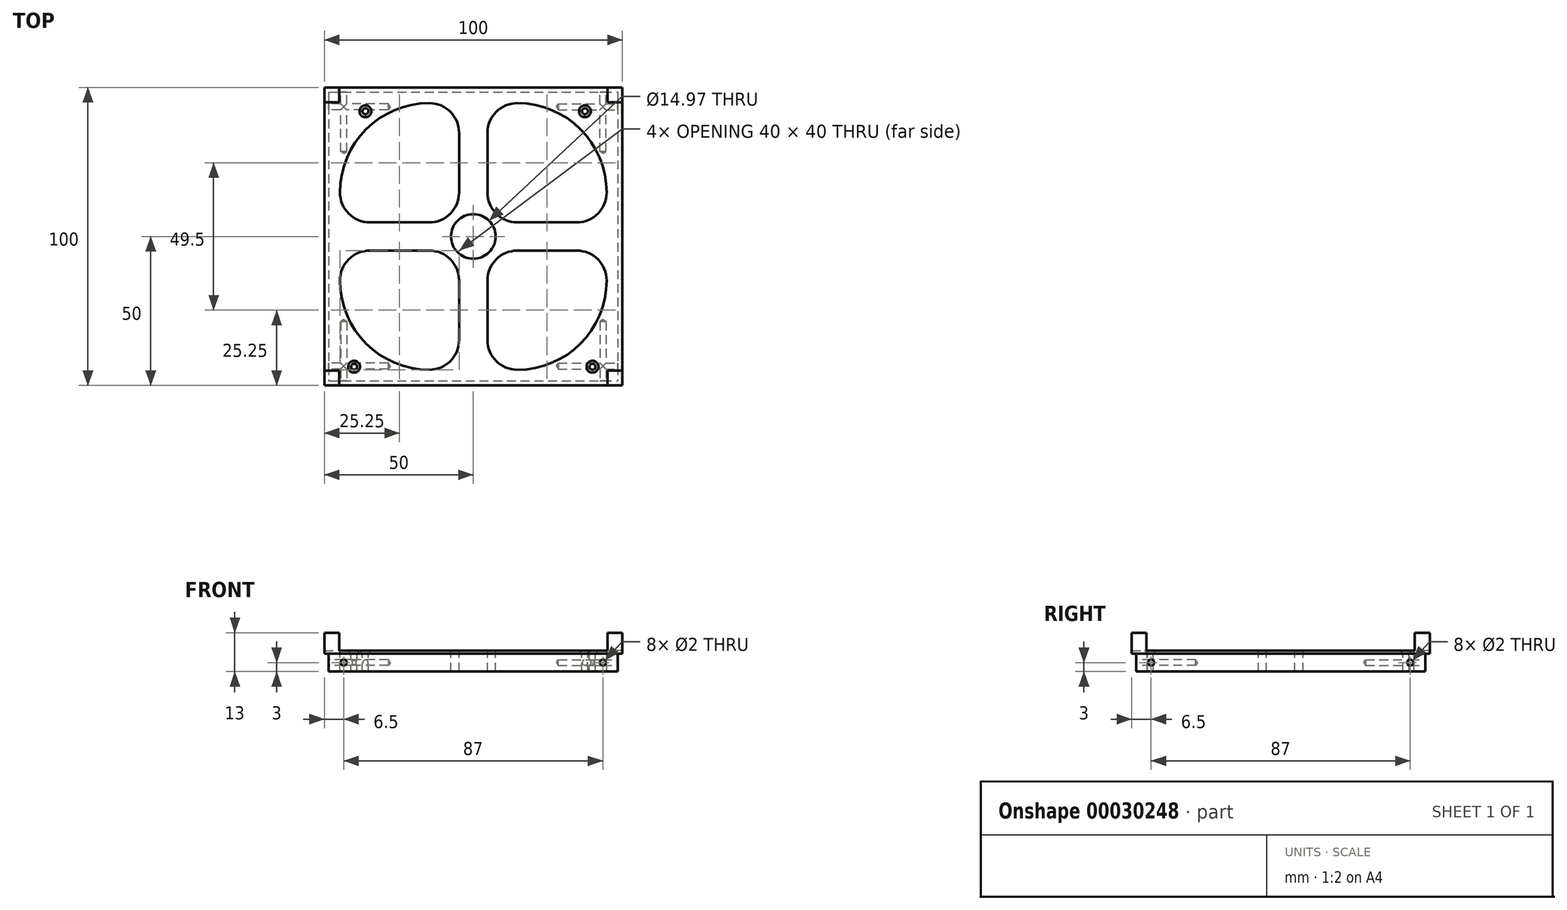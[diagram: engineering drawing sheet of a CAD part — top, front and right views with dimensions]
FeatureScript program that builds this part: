
annotation { "Feature Type Name" : "Feature", "Feature Type Description" : "" }
export const myFeature = defineFeature(function(context is Context, id is Id, definition is map)
    precondition{}
    {
        {
            var Q0;
            Q0=qCreatedBy(makeId("Top.planeOp"),FACE);
            var sketch = newSketch(context, id + "F0", { "sketchPlane" : qUnion([Q0])});
            skLineSegment(sketch, "E0.rect.bottom", {"start": v(-50, 50) * mm, "end": v(50, 50) * mm});
            skLineSegment(sketch, "E0.rect.top", {"start": v(-50, -50) * mm, "end": v(50, -50) * mm});
            skLineSegment(sketch, "E0.rect.left", {"start": v(-50, 50) * mm, "end": v(-50, -50) * mm});
            skLineSegment(sketch, "E0.rect.right", {"start": v(50, 50) * mm, "end": v(50, -50) * mm});
            skPoint(sketch, "E0.rect.middle", {"position": v(0, 0) * mm});
            skLineSegment(sketch, "E1.rect.bottom", {"start": v(-48.5, 48.5) * mm, "end": v(48.5, 48.5) * mm});
            skLineSegment(sketch, "E1.rect.top", {"start": v(-48.5, -48.5) * mm, "end": v(48.5, -48.5) * mm});
            skLineSegment(sketch, "E1.rect.left", {"start": v(-48.5, 48.5) * mm, "end": v(-48.5, -48.5) * mm});
            skLineSegment(sketch, "E1.rect.right", {"start": v(48.5, 48.5) * mm, "end": v(48.5, -48.5) * mm});
            skLineSegment(sketch, "E2.rect.bottom", {"start": v(-14.75, 4.75) * mm, "end": v(-34.75, 4.75) * mm});
            skLineSegment(sketch, "E2.rect.top", {"start": v(-14.75, 44.75) * mm, "end": v(-14.75, 44.75) * mm});
            skLineSegment(sketch, "E2.rect.left", {"start": v(-4.75, 14.75) * mm, "end": v(-4.75, 34.75) * mm});
            skLineSegment(sketch, "E2.rect.right", {"start": v(-44.75, 14.75) * mm, "end": v(-44.75, 14.75) * mm});
            skPoint(sketch, "E2.rect.middle", {"position": v(-24.75, 24.75) * mm});
            skPoint(sketch, "E3.visualSharp", {"position": v(-44.75, 44.75) * mm});
            skArc(sketch, "E3.filletArc", {"start": v(-14.75, 44.75) * mm, "mid": v(-35.96, 35.96) * mm, "end": v(-44.75, 14.75) * mm});
            skPoint(sketch, "E4.visualSharp", {"position": v(-4.75, 44.75) * mm});
            skArc(sketch, "E4.filletArc", {"start": v(-4.75, 34.75) * mm, "mid": v(-7.68, 41.82) * mm, "end": v(-14.75, 44.75) * mm});
            skPoint(sketch, "E5.visualSharp", {"position": v(-4.75, 4.75) * mm});
            skArc(sketch, "E5.filletArc", {"start": v(-14.75, 4.75) * mm, "mid": v(-7.68, 7.68) * mm, "end": v(-4.75, 14.75) * mm});
            skPoint(sketch, "E6.visualSharp", {"position": v(-44.75, 4.75) * mm});
            skArc(sketch, "E6.filletArc", {"start": v(-44.75, 14.75) * mm, "mid": v(-41.82, 7.68) * mm, "end": v(-34.75, 4.75) * mm});
            skLineSegment(sketch, "E7.MirrorCS", {"start": v(4.75, 14.75) * mm, "end": v(4.75, 34.75) * mm});
            skArc(sketch, "E8.MirrorCS", {"start": v(4.75, 34.75) * mm, "mid": v(7.68, 41.82) * mm, "end": v(14.75, 44.75) * mm});
            skLineSegment(sketch, "E9.MirrorCS", {"start": v(14.75, 44.75) * mm, "end": v(14.75, 44.75) * mm});
            skArc(sketch, "E10.MirrorCS", {"start": v(14.75, 44.75) * mm, "mid": v(35.96, 35.96) * mm, "end": v(44.75, 14.75) * mm});
            skLineSegment(sketch, "E11.MirrorCS", {"start": v(44.75, 14.75) * mm, "end": v(44.75, 14.75) * mm});
            skArc(sketch, "E12.MirrorCS", {"start": v(44.75, 14.75) * mm, "mid": v(41.82, 7.68) * mm, "end": v(34.75, 4.75) * mm});
            skLineSegment(sketch, "E13.MirrorCS", {"start": v(14.75, 4.75) * mm, "end": v(34.75, 4.75) * mm});
            skArc(sketch, "E14.MirrorCS", {"start": v(14.75, 4.75) * mm, "mid": v(7.68, 7.68) * mm, "end": v(4.75, 14.75) * mm});
            skPoint(sketch, "E15.MirrorP", {"position": v(24.75, 24.75) * mm});
            skArc(sketch, "E16.MirrorCS", {"start": v(14.75, -4.75) * mm, "mid": v(7.68, -7.68) * mm, "end": v(4.75, -14.75) * mm});
            skLineSegment(sketch, "E17.MirrorCS", {"start": v(4.75, -14.75) * mm, "end": v(4.75, -34.75) * mm});
            skArc(sketch, "E18.MirrorCS", {"start": v(4.75, -34.75) * mm, "mid": v(7.68, -41.82) * mm, "end": v(14.75, -44.75) * mm});
            skLineSegment(sketch, "E19.MirrorCS", {"start": v(14.75, -44.75) * mm, "end": v(14.75, -44.75) * mm});
            skArc(sketch, "E20.MirrorCS", {"start": v(14.75, -44.75) * mm, "mid": v(35.96, -35.96) * mm, "end": v(44.75, -14.75) * mm});
            skLineSegment(sketch, "E21.MirrorCS", {"start": v(44.75, -14.75) * mm, "end": v(44.75, -14.75) * mm});
            skArc(sketch, "E22.MirrorCS", {"start": v(44.75, -14.75) * mm, "mid": v(41.82, -7.68) * mm, "end": v(34.75, -4.75) * mm});
            skLineSegment(sketch, "E23.MirrorCS", {"start": v(14.75, -4.75) * mm, "end": v(34.75, -4.75) * mm});
            skPoint(sketch, "E24.MirrorP", {"position": v(24.75, -24.75) * mm});
            skLineSegment(sketch, "E25.MirrorCS", {"start": v(-4.75, -14.75) * mm, "end": v(-4.75, -34.75) * mm});
            skArc(sketch, "E26.MirrorCS", {"start": v(-14.75, -4.75) * mm, "mid": v(-7.68, -7.68) * mm, "end": v(-4.75, -14.75) * mm});
            skLineSegment(sketch, "E27.MirrorCS", {"start": v(-14.75, -4.75) * mm, "end": v(-34.75, -4.75) * mm});
            skArc(sketch, "E28.MirrorCS", {"start": v(-44.75, -14.75) * mm, "mid": v(-41.82, -7.68) * mm, "end": v(-34.75, -4.75) * mm});
            skLineSegment(sketch, "E29.MirrorCS", {"start": v(-44.75, -14.75) * mm, "end": v(-44.75, -14.75) * mm});
            skArc(sketch, "E30.MirrorCS", {"start": v(-14.75, -44.75) * mm, "mid": v(-35.96, -35.96) * mm, "end": v(-44.75, -14.75) * mm});
            skLineSegment(sketch, "E31.MirrorCS", {"start": v(-14.75, -44.75) * mm, "end": v(-14.75, -44.75) * mm});
            skArc(sketch, "E32.MirrorCS", {"start": v(-4.75, -34.75) * mm, "mid": v(-7.68, -41.82) * mm, "end": v(-14.75, -44.75) * mm});
            skPoint(sketch, "E33.MirrorP", {"position": v(-24.75, -24.75) * mm});
            skCircle(sketch, "E34", {"center": v(0, 0) * mm, "radius": 7.48 * mm});
            skPoint(sketch, "E35", {"position": v(-40, -42.87) * mm});
            skPoint(sketch, "E36.MirrorP", {"position": v(40, -42.87) * mm});
            skPoint(sketch, "E37", {"position": v(-36.2, 42.87) * mm});
            skPoint(sketch, "E38.positionSnap0", {"position": v(7.68, 41.82) * mm});
            skPoint(sketch, "E39", {"position": v(37.47, 42.87) * mm});
            skSolve(sketch);
        }
        {
            var Q0;
            Q0=makeQuery(id+"F0.imprint","IMPRINT",FACE,{"disambiguationData":[TD([[makeQuery(id+"F0.imprint","IMPRINT",EDGE,{"derivedFrom":sQuery(id+"F0.wireOp",EDGE,"E1.rect.bottom")}),-1.0]])]});
            extrude(context, id + "F1", {"entities" : qUnion([Q0]), "oppositeDirection" : true, "depth" : 6 * mm});
        }
        {
            var Q0;
            Q0=qSketchRegion(id+"F0",true);
            var Q1;
            Q1=makeQuery(id+"F1.opExtrude","CAP_FACE",FACE,{"disambiguationData":[OSD([sQuery(id+"F0.wireOp",EDGE,"E1.rect.bottom"),sQuery(id+"F0.wireOp",EDGE,"E1.rect.top"),sQuery(id+"F0.wireOp",EDGE,"E1.rect.left"),sQuery(id+"F0.wireOp",EDGE,"E1.rect.right"),sQuery(id+"F0.wireOp",EDGE,"E2.rect.bottom"),sQuery(id+"F0.wireOp",EDGE,"E2.rect.top"),sQuery(id+"F0.wireOp",EDGE,"E2.rect.left"),sQuery(id+"F0.wireOp",EDGE,"E2.rect.right"),sQuery(id+"F0.wireOp",EDGE,"d764ca65-7f6a-4e13-98eb-a7907a3d072d0.MirrorCS"),sQuery(id+"F0.wireOp",EDGE,"4e8c5bec-c53d-4312-8259-349e49f543fe0.MirrorCS"),sQuery(id+"F0.wireOp",EDGE,"d6a0bf7c-e4bc-484e-b3d5-183d898144500.MirrorCS"),sQuery(id+"F0.wireOp",EDGE,"45a758ec-378c-46c5-b086-a70cc1cacffd0.MirrorCS"),sQuery(id+"F0.wireOp",EDGE,"a64d5360-d78c-41ef-9f44-8c8436a09bba0.MirrorCS"),sQuery(id+"F0.wireOp",EDGE,"c998a958-b69a-464e-a296-dd7f6d349ec80.MirrorCS"),sQuery(id+"F0.wireOp",EDGE,"a4bf1b2a-a2f4-4ab3-9d73-85797b196d270.MirrorCS"),sQuery(id+"F0.wireOp",EDGE,"ecd2f3fb-4ea3-4913-80f4-94ebebe2d04e0.MirrorCS"),sQuery(id+"F0.wireOp",EDGE,"085a2cb5-2e3f-4cc3-a5b9-01c6e75669f10.MirrorCS"),sQuery(id+"F0.wireOp",EDGE,"73d67a52-dadc-4bd6-8141-d25047cb753b0.MirrorCS"),sQuery(id+"F0.wireOp",EDGE,"8f6832c0-858d-4205-8574-29f35786d1620.MirrorCS"),sQuery(id+"F0.wireOp",EDGE,"ecc9a695-4792-4055-9804-abf58933c5b20.MirrorCS")])],"isStart":false});
            extrude(context, id + "F2", {"entities" : qUnion([Q0, Q1]), "operationType" : NewBodyOperationType.ADD, "oppositeDirection" : true, "depth" : 1 * mm});
        }
        {
            var Q0;
            {var subQ0=sQuery(id+"F0.wireOp",EDGE,"E1.rect.bottom");Q0=makeQuery(id+"F2.boolean.opBoolean","MERGE",FACE,{"derivedFrom":[makeQuery(id+"F1.opExtrude","SWEPT_FACE",FACE,{"disambiguationData":[OSD([subQ0])]}),makeQuery(id+"F2.opExtrude","SWEPT_FACE",FACE,{"disambiguationData":[OSD([subQ0]),TDD([makeQuery(id+"F1.opExtrude","CAP_EDGE",EDGE,{"disambiguationData":[OSD([subQ0])],"isStart":false})])]})]});}
            var sketch = newSketch(context, id + "F3", { "sketchPlane" : qUnion([Q0])});
            skPoint(sketch, "E40", {"position": v(-43.5, -4) * mm});
            skPoint(sketch, "E41.MirrorP", {"position": v(43.5, -4) * mm});
            skSolve(sketch);
        }
        {
            var Q0;
            Q0=sQuery(id+"F3.wireOp",VERTEX,"E40");
            var Q1;
            Q1=sQuery(id+"F3.wireOp",VERTEX,"E41.MirrorP");
            var Q2;
            Q2=makeQuery(id+"F1.opExtrude","SWEPT_BODY",BODY,{"disambiguationData":[OSD([sQuery(id+"F0.wireOp",EDGE,"E1.rect.bottom"),sQuery(id+"F0.wireOp",EDGE,"E1.rect.top"),sQuery(id+"F0.wireOp",EDGE,"E1.rect.left"),sQuery(id+"F0.wireOp",EDGE,"E1.rect.right"),sQuery(id+"F0.wireOp",EDGE,"E2.rect.bottom"),sQuery(id+"F0.wireOp",EDGE,"E2.rect.top"),sQuery(id+"F0.wireOp",EDGE,"E2.rect.left"),sQuery(id+"F0.wireOp",EDGE,"E2.rect.right"),sQuery(id+"F0.wireOp",EDGE,"E3.filletArc"),sQuery(id+"F0.wireOp",EDGE,"E4.filletArc"),sQuery(id+"F0.wireOp",EDGE,"E5.filletArc"),sQuery(id+"F0.wireOp",EDGE,"E6.filletArc"),sQuery(id+"F0.wireOp",EDGE,"E7.MirrorCS"),sQuery(id+"F0.wireOp",EDGE,"E8.MirrorCS"),sQuery(id+"F0.wireOp",EDGE,"E9.MirrorCS"),sQuery(id+"F0.wireOp",EDGE,"E10.MirrorCS"),sQuery(id+"F0.wireOp",EDGE,"E11.MirrorCS"),sQuery(id+"F0.wireOp",EDGE,"E12.MirrorCS"),sQuery(id+"F0.wireOp",EDGE,"E13.MirrorCS"),sQuery(id+"F0.wireOp",EDGE,"E14.MirrorCS"),sQuery(id+"F0.wireOp",EDGE,"E16.MirrorCS"),sQuery(id+"F0.wireOp",EDGE,"E17.MirrorCS"),sQuery(id+"F0.wireOp",EDGE,"E18.MirrorCS"),sQuery(id+"F0.wireOp",EDGE,"E19.MirrorCS"),sQuery(id+"F0.wireOp",EDGE,"E20.MirrorCS"),sQuery(id+"F0.wireOp",EDGE,"E21.MirrorCS"),sQuery(id+"F0.wireOp",EDGE,"E22.MirrorCS"),sQuery(id+"F0.wireOp",EDGE,"E23.MirrorCS"),sQuery(id+"F0.wireOp",EDGE,"E25.MirrorCS"),sQuery(id+"F0.wireOp",EDGE,"E26.MirrorCS"),sQuery(id+"F0.wireOp",EDGE,"E27.MirrorCS"),sQuery(id+"F0.wireOp",EDGE,"E28.MirrorCS"),sQuery(id+"F0.wireOp",EDGE,"E29.MirrorCS"),sQuery(id+"F0.wireOp",EDGE,"E30.MirrorCS"),sQuery(id+"F0.wireOp",EDGE,"E31.MirrorCS"),sQuery(id+"F0.wireOp",EDGE,"E32.MirrorCS")])]});
            hole(context, id + "F4", {"style" : HoleStyle.SIMPLE, "holeDiameter" : 2 * mm, "endStyle" : HoleEndStyle.BLIND, "holeDepth" : 20 * mm, "locations" : qUnion([Q0, Q1]), "scope" : qUnion([Q2])});
        }
        {
            var Q0;
            {var subQ0=sQuery(id+"F0.wireOp",EDGE,"E1.rect.left");Q0=makeQuery(id+"F2.boolean.opBoolean","MERGE",FACE,{"derivedFrom":[makeQuery(id+"F1.opExtrude","SWEPT_FACE",FACE,{"disambiguationData":[OSD([subQ0])]}),makeQuery(id+"F2.opExtrude","SWEPT_FACE",FACE,{"disambiguationData":[OSD([subQ0]),TDD([makeQuery(id+"F1.opExtrude","CAP_EDGE",EDGE,{"disambiguationData":[OSD([subQ0])],"isStart":false})])]})]});}
            var sketch = newSketch(context, id + "F5", { "sketchPlane" : qUnion([Q0])});
            skPoint(sketch, "E42", {"position": v(-43.5, -4) * mm});
            skPoint(sketch, "E43.MirrorP", {"position": v(43.5, -4) * mm});
            skSolve(sketch);
        }
        {
            var Q0;
            Q0=sQuery(id+"F5.wireOp",VERTEX,"E42");
            var Q1;
            Q1=sQuery(id+"F5.wireOp",VERTEX,"E43.MirrorP");
            var Q2;
            Q2=makeQuery(id+"F1.opExtrude","SWEPT_BODY",BODY,{"disambiguationData":[OSD([sQuery(id+"F0.wireOp",EDGE,"E1.rect.bottom"),sQuery(id+"F0.wireOp",EDGE,"E1.rect.top"),sQuery(id+"F0.wireOp",EDGE,"E1.rect.left"),sQuery(id+"F0.wireOp",EDGE,"E1.rect.right"),sQuery(id+"F0.wireOp",EDGE,"E2.rect.bottom"),sQuery(id+"F0.wireOp",EDGE,"E2.rect.top"),sQuery(id+"F0.wireOp",EDGE,"E2.rect.left"),sQuery(id+"F0.wireOp",EDGE,"E2.rect.right"),sQuery(id+"F0.wireOp",EDGE,"E3.filletArc"),sQuery(id+"F0.wireOp",EDGE,"E4.filletArc"),sQuery(id+"F0.wireOp",EDGE,"E5.filletArc"),sQuery(id+"F0.wireOp",EDGE,"E6.filletArc"),sQuery(id+"F0.wireOp",EDGE,"E7.MirrorCS"),sQuery(id+"F0.wireOp",EDGE,"E8.MirrorCS"),sQuery(id+"F0.wireOp",EDGE,"E9.MirrorCS"),sQuery(id+"F0.wireOp",EDGE,"E10.MirrorCS"),sQuery(id+"F0.wireOp",EDGE,"E11.MirrorCS"),sQuery(id+"F0.wireOp",EDGE,"E12.MirrorCS"),sQuery(id+"F0.wireOp",EDGE,"E13.MirrorCS"),sQuery(id+"F0.wireOp",EDGE,"E14.MirrorCS"),sQuery(id+"F0.wireOp",EDGE,"E16.MirrorCS"),sQuery(id+"F0.wireOp",EDGE,"E17.MirrorCS"),sQuery(id+"F0.wireOp",EDGE,"E18.MirrorCS"),sQuery(id+"F0.wireOp",EDGE,"E19.MirrorCS"),sQuery(id+"F0.wireOp",EDGE,"E20.MirrorCS"),sQuery(id+"F0.wireOp",EDGE,"E21.MirrorCS"),sQuery(id+"F0.wireOp",EDGE,"E22.MirrorCS"),sQuery(id+"F0.wireOp",EDGE,"E23.MirrorCS"),sQuery(id+"F0.wireOp",EDGE,"E25.MirrorCS"),sQuery(id+"F0.wireOp",EDGE,"E26.MirrorCS"),sQuery(id+"F0.wireOp",EDGE,"E27.MirrorCS"),sQuery(id+"F0.wireOp",EDGE,"E28.MirrorCS"),sQuery(id+"F0.wireOp",EDGE,"E29.MirrorCS"),sQuery(id+"F0.wireOp",EDGE,"E30.MirrorCS"),sQuery(id+"F0.wireOp",EDGE,"E31.MirrorCS"),sQuery(id+"F0.wireOp",EDGE,"E32.MirrorCS")])]});
            hole(context, id + "F6", {"style" : HoleStyle.SIMPLE, "holeDiameter" : 2 * mm, "endStyle" : HoleEndStyle.BLIND, "holeDepth" : 20 * mm, "locations" : qUnion([Q0, Q1]), "scope" : qUnion([Q2])});
        }
        {
            var Q0;
            {var subQ0=sQuery(id+"F0.wireOp",EDGE,"E1.rect.top");Q0=makeQuery(id+"F2.boolean.opBoolean","MERGE",FACE,{"derivedFrom":[makeQuery(id+"F1.opExtrude","SWEPT_FACE",FACE,{"disambiguationData":[OSD([subQ0])]}),makeQuery(id+"F2.opExtrude","SWEPT_FACE",FACE,{"disambiguationData":[OSD([subQ0]),TDD([makeQuery(id+"F1.opExtrude","CAP_EDGE",EDGE,{"disambiguationData":[OSD([subQ0])],"isStart":false})])]})]});}
            var sketch = newSketch(context, id + "F7", { "sketchPlane" : qUnion([Q0])});
            skPoint(sketch, "E44", {"position": v(-43.5, -4) * mm});
            skPoint(sketch, "E45.MirrorP", {"position": v(43.5, -4) * mm});
            skSolve(sketch);
        }
        {
            var Q0;
            Q0=sQuery(id+"F7.wireOp",VERTEX,"E44");
            var Q1;
            Q1=sQuery(id+"F7.wireOp",VERTEX,"E45.MirrorP");
            var Q2;
            Q2=makeQuery(id+"F1.opExtrude","SWEPT_BODY",BODY,{"disambiguationData":[OSD([sQuery(id+"F0.wireOp",EDGE,"E1.rect.bottom"),sQuery(id+"F0.wireOp",EDGE,"E1.rect.top"),sQuery(id+"F0.wireOp",EDGE,"E1.rect.left"),sQuery(id+"F0.wireOp",EDGE,"E1.rect.right"),sQuery(id+"F0.wireOp",EDGE,"E2.rect.bottom"),sQuery(id+"F0.wireOp",EDGE,"E2.rect.top"),sQuery(id+"F0.wireOp",EDGE,"E2.rect.left"),sQuery(id+"F0.wireOp",EDGE,"E2.rect.right"),sQuery(id+"F0.wireOp",EDGE,"E3.filletArc"),sQuery(id+"F0.wireOp",EDGE,"E4.filletArc"),sQuery(id+"F0.wireOp",EDGE,"E5.filletArc"),sQuery(id+"F0.wireOp",EDGE,"E6.filletArc"),sQuery(id+"F0.wireOp",EDGE,"E7.MirrorCS"),sQuery(id+"F0.wireOp",EDGE,"E8.MirrorCS"),sQuery(id+"F0.wireOp",EDGE,"E9.MirrorCS"),sQuery(id+"F0.wireOp",EDGE,"E10.MirrorCS"),sQuery(id+"F0.wireOp",EDGE,"E11.MirrorCS"),sQuery(id+"F0.wireOp",EDGE,"E12.MirrorCS"),sQuery(id+"F0.wireOp",EDGE,"E13.MirrorCS"),sQuery(id+"F0.wireOp",EDGE,"E14.MirrorCS"),sQuery(id+"F0.wireOp",EDGE,"E16.MirrorCS"),sQuery(id+"F0.wireOp",EDGE,"E17.MirrorCS"),sQuery(id+"F0.wireOp",EDGE,"E18.MirrorCS"),sQuery(id+"F0.wireOp",EDGE,"E19.MirrorCS"),sQuery(id+"F0.wireOp",EDGE,"E20.MirrorCS"),sQuery(id+"F0.wireOp",EDGE,"E21.MirrorCS"),sQuery(id+"F0.wireOp",EDGE,"E22.MirrorCS"),sQuery(id+"F0.wireOp",EDGE,"E23.MirrorCS"),sQuery(id+"F0.wireOp",EDGE,"E25.MirrorCS"),sQuery(id+"F0.wireOp",EDGE,"E26.MirrorCS"),sQuery(id+"F0.wireOp",EDGE,"E27.MirrorCS"),sQuery(id+"F0.wireOp",EDGE,"E28.MirrorCS"),sQuery(id+"F0.wireOp",EDGE,"E29.MirrorCS"),sQuery(id+"F0.wireOp",EDGE,"E30.MirrorCS"),sQuery(id+"F0.wireOp",EDGE,"E31.MirrorCS"),sQuery(id+"F0.wireOp",EDGE,"E32.MirrorCS")])]});
            hole(context, id + "F8", {"style" : HoleStyle.SIMPLE, "holeDiameter" : 2 * mm, "endStyle" : HoleEndStyle.BLIND, "holeDepth" : 20 * mm, "locations" : qUnion([Q0, Q1]), "scope" : qUnion([Q2])});
        }
        {
            var Q0;
            {var subQ0=sQuery(id+"F0.wireOp",EDGE,"E1.rect.right");Q0=makeQuery(id+"F2.boolean.opBoolean","MERGE",FACE,{"derivedFrom":[makeQuery(id+"F1.opExtrude","SWEPT_FACE",FACE,{"disambiguationData":[OSD([subQ0])]}),makeQuery(id+"F2.opExtrude","SWEPT_FACE",FACE,{"disambiguationData":[OSD([subQ0]),TDD([makeQuery(id+"F1.opExtrude","CAP_EDGE",EDGE,{"disambiguationData":[OSD([subQ0])],"isStart":false})])]})]});}
            var sketch = newSketch(context, id + "F9", { "sketchPlane" : qUnion([Q0])});
            skPoint(sketch, "E46", {"position": v(-43.5, -4) * mm});
            skPoint(sketch, "E47.MirrorP", {"position": v(43.5, -4) * mm});
            skSolve(sketch);
        }
        {
            var Q0;
            Q0=sQuery(id+"F9.wireOp",VERTEX,"E46");
            var Q1;
            Q1=sQuery(id+"F9.wireOp",VERTEX,"E47.MirrorP");
            var Q2;
            Q2=makeQuery(id+"F1.opExtrude","SWEPT_BODY",BODY,{"disambiguationData":[OSD([sQuery(id+"F0.wireOp",EDGE,"E1.rect.bottom"),sQuery(id+"F0.wireOp",EDGE,"E1.rect.top"),sQuery(id+"F0.wireOp",EDGE,"E1.rect.left"),sQuery(id+"F0.wireOp",EDGE,"E1.rect.right"),sQuery(id+"F0.wireOp",EDGE,"E2.rect.bottom"),sQuery(id+"F0.wireOp",EDGE,"E2.rect.top"),sQuery(id+"F0.wireOp",EDGE,"E2.rect.left"),sQuery(id+"F0.wireOp",EDGE,"E2.rect.right"),sQuery(id+"F0.wireOp",EDGE,"E3.filletArc"),sQuery(id+"F0.wireOp",EDGE,"E4.filletArc"),sQuery(id+"F0.wireOp",EDGE,"E5.filletArc"),sQuery(id+"F0.wireOp",EDGE,"E6.filletArc"),sQuery(id+"F0.wireOp",EDGE,"E7.MirrorCS"),sQuery(id+"F0.wireOp",EDGE,"E8.MirrorCS"),sQuery(id+"F0.wireOp",EDGE,"E9.MirrorCS"),sQuery(id+"F0.wireOp",EDGE,"E10.MirrorCS"),sQuery(id+"F0.wireOp",EDGE,"E11.MirrorCS"),sQuery(id+"F0.wireOp",EDGE,"E12.MirrorCS"),sQuery(id+"F0.wireOp",EDGE,"E13.MirrorCS"),sQuery(id+"F0.wireOp",EDGE,"E14.MirrorCS"),sQuery(id+"F0.wireOp",EDGE,"E16.MirrorCS"),sQuery(id+"F0.wireOp",EDGE,"E17.MirrorCS"),sQuery(id+"F0.wireOp",EDGE,"E18.MirrorCS"),sQuery(id+"F0.wireOp",EDGE,"E19.MirrorCS"),sQuery(id+"F0.wireOp",EDGE,"E20.MirrorCS"),sQuery(id+"F0.wireOp",EDGE,"E21.MirrorCS"),sQuery(id+"F0.wireOp",EDGE,"E22.MirrorCS"),sQuery(id+"F0.wireOp",EDGE,"E23.MirrorCS"),sQuery(id+"F0.wireOp",EDGE,"E25.MirrorCS"),sQuery(id+"F0.wireOp",EDGE,"E26.MirrorCS"),sQuery(id+"F0.wireOp",EDGE,"E27.MirrorCS"),sQuery(id+"F0.wireOp",EDGE,"E28.MirrorCS"),sQuery(id+"F0.wireOp",EDGE,"E29.MirrorCS"),sQuery(id+"F0.wireOp",EDGE,"E30.MirrorCS"),sQuery(id+"F0.wireOp",EDGE,"E31.MirrorCS"),sQuery(id+"F0.wireOp",EDGE,"E32.MirrorCS")])]});
            hole(context, id + "F10", {"style" : HoleStyle.SIMPLE, "holeDiameter" : 2 * mm, "endStyle" : HoleEndStyle.BLIND, "holeDepth" : 20 * mm, "locations" : qUnion([Q0, Q1]), "scope" : qUnion([Q2])});
        }
        {
            var Q0;
            {var subQ0=sQuery(id+"F0.wireOp",EDGE,"E1.rect.bottom");var subQ1=sQuery(id+"F0.wireOp",EDGE,"E1.rect.top");var subQ2=sQuery(id+"F0.wireOp",EDGE,"E1.rect.left");var subQ3=sQuery(id+"F0.wireOp",EDGE,"E1.rect.right");Q0=makeQuery(id+"F2.boolean.opBoolean","MERGE",FACE,{"derivedFrom":[makeQuery(id+"F1.opExtrude","CAP_FACE",FACE,{"disambiguationData":[OSD([subQ0,subQ1,subQ2,subQ3,sQuery(id+"F0.wireOp",EDGE,"E2.rect.bottom"),sQuery(id+"F0.wireOp",EDGE,"E2.rect.top"),sQuery(id+"F0.wireOp",EDGE,"E2.rect.left"),sQuery(id+"F0.wireOp",EDGE,"E2.rect.right"),sQuery(id+"F0.wireOp",EDGE,"E3.filletArc"),sQuery(id+"F0.wireOp",EDGE,"E4.filletArc"),sQuery(id+"F0.wireOp",EDGE,"E5.filletArc"),sQuery(id+"F0.wireOp",EDGE,"E6.filletArc"),sQuery(id+"F0.wireOp",EDGE,"E7.MirrorCS"),sQuery(id+"F0.wireOp",EDGE,"E8.MirrorCS"),sQuery(id+"F0.wireOp",EDGE,"E9.MirrorCS"),sQuery(id+"F0.wireOp",EDGE,"E10.MirrorCS"),sQuery(id+"F0.wireOp",EDGE,"E11.MirrorCS"),sQuery(id+"F0.wireOp",EDGE,"E12.MirrorCS"),sQuery(id+"F0.wireOp",EDGE,"E13.MirrorCS"),sQuery(id+"F0.wireOp",EDGE,"E14.MirrorCS"),sQuery(id+"F0.wireOp",EDGE,"E16.MirrorCS"),sQuery(id+"F0.wireOp",EDGE,"E17.MirrorCS"),sQuery(id+"F0.wireOp",EDGE,"E18.MirrorCS"),sQuery(id+"F0.wireOp",EDGE,"E19.MirrorCS"),sQuery(id+"F0.wireOp",EDGE,"E20.MirrorCS"),sQuery(id+"F0.wireOp",EDGE,"E21.MirrorCS"),sQuery(id+"F0.wireOp",EDGE,"E22.MirrorCS"),sQuery(id+"F0.wireOp",EDGE,"E23.MirrorCS"),sQuery(id+"F0.wireOp",EDGE,"E25.MirrorCS"),sQuery(id+"F0.wireOp",EDGE,"E26.MirrorCS"),sQuery(id+"F0.wireOp",EDGE,"E27.MirrorCS"),sQuery(id+"F0.wireOp",EDGE,"E28.MirrorCS"),sQuery(id+"F0.wireOp",EDGE,"E29.MirrorCS"),sQuery(id+"F0.wireOp",EDGE,"E30.MirrorCS"),sQuery(id+"F0.wireOp",EDGE,"E31.MirrorCS"),sQuery(id+"F0.wireOp",EDGE,"E32.MirrorCS")])],"isStart":true}),makeQuery(id+"F2.opExtrude","CAP_FACE",FACE,{"disambiguationData":[OSD([sQuery(id+"F0.wireOp",EDGE,"E0.rect.bottom"),sQuery(id+"F0.wireOp",EDGE,"E0.rect.top"),sQuery(id+"F0.wireOp",EDGE,"E0.rect.left"),sQuery(id+"F0.wireOp",EDGE,"E0.rect.right"),subQ0,subQ1,subQ2,subQ3])],"isStart":true})]});}
            var sketch = newSketch(context, id + "F11", { "sketchPlane" : qUnion([Q0])});
            skPoint(sketch, "E48", {"position": v(-36.2, -129.45) * mm});
            skPoint(sketch, "E49", {"position": v(40, -43.72) * mm});
            skPoint(sketch, "E50", {"position": v(37.47, -129.45) * mm});
            skPoint(sketch, "E51", {"position": v(-40, -43.72) * mm});
            skPoint(sketch, "E52", {"position": v(-36.2, 42.01) * mm});
            skPoint(sketch, "E53", {"position": v(37.46, 42.01) * mm});
            skLineSegment(sketch, "E54.bottom", {"start": v(50, 50) * mm, "end": v(45, 50) * mm});
            skLineSegment(sketch, "E54.top", {"start": v(50, 45) * mm, "end": v(45, 45) * mm});
            skLineSegment(sketch, "E54.left", {"start": v(50, 50) * mm, "end": v(50, 45) * mm});
            skLineSegment(sketch, "E54.right", {"start": v(45, 50) * mm, "end": v(45, 45) * mm});
            skLineSegment(sketch, "E55.MirrorCS", {"start": v(-45, 50) * mm, "end": v(-45, 45) * mm});
            skLineSegment(sketch, "E56.MirrorCS", {"start": v(-50, 50) * mm, "end": v(-50, 45) * mm});
            skLineSegment(sketch, "E57.MirrorCS", {"start": v(-50, 45) * mm, "end": v(-45, 45) * mm});
            skLineSegment(sketch, "E58.MirrorCS", {"start": v(-50, 50) * mm, "end": v(-45, 50) * mm});
            skLineSegment(sketch, "E59.MirrorCS", {"start": v(50, -45) * mm, "end": v(45, -45) * mm});
            skLineSegment(sketch, "E60.MirrorCS", {"start": v(50, -50) * mm, "end": v(45, -50) * mm});
            skLineSegment(sketch, "E61.MirrorCS", {"start": v(50, -50) * mm, "end": v(50, -45) * mm});
            skLineSegment(sketch, "E62.MirrorCS", {"start": v(45, -50) * mm, "end": v(45, -45) * mm});
            skLineSegment(sketch, "E63.MirrorCS", {"start": v(-50, -50) * mm, "end": v(-50, -45) * mm});
            skLineSegment(sketch, "E64.MirrorCS", {"start": v(-45, -50) * mm, "end": v(-45, -45) * mm});
            skLineSegment(sketch, "E65.MirrorCS", {"start": v(-50, -45) * mm, "end": v(-45, -45) * mm});
            skLineSegment(sketch, "E66.MirrorCS", {"start": v(-50, -50) * mm, "end": v(-45, -50) * mm});
            skSolve(sketch);
        }
        {
            var Q0;
            Q0=sQuery(id+"F11.wireOp",VERTEX,"E53");
            var Q1;
            Q1=sQuery(id+"F11.wireOp",VERTEX,"E52");
            var Q2;
            Q2=sQuery(id+"F11.wireOp",VERTEX,"E49");
            var Q3;
            Q3=sQuery(id+"F11.wireOp",VERTEX,"E51");
            var Q4;
            Q4=makeQuery(id+"F1.opExtrude","SWEPT_BODY",BODY,{"disambiguationData":[OSD([sQuery(id+"F0.wireOp",EDGE,"E1.rect.bottom"),sQuery(id+"F0.wireOp",EDGE,"E1.rect.top"),sQuery(id+"F0.wireOp",EDGE,"E1.rect.left"),sQuery(id+"F0.wireOp",EDGE,"E1.rect.right"),sQuery(id+"F0.wireOp",EDGE,"E2.rect.bottom"),sQuery(id+"F0.wireOp",EDGE,"E2.rect.top"),sQuery(id+"F0.wireOp",EDGE,"E2.rect.left"),sQuery(id+"F0.wireOp",EDGE,"E2.rect.right"),sQuery(id+"F0.wireOp",EDGE,"E3.filletArc"),sQuery(id+"F0.wireOp",EDGE,"E4.filletArc"),sQuery(id+"F0.wireOp",EDGE,"E5.filletArc"),sQuery(id+"F0.wireOp",EDGE,"E6.filletArc"),sQuery(id+"F0.wireOp",EDGE,"E7.MirrorCS"),sQuery(id+"F0.wireOp",EDGE,"E8.MirrorCS"),sQuery(id+"F0.wireOp",EDGE,"E9.MirrorCS"),sQuery(id+"F0.wireOp",EDGE,"E10.MirrorCS"),sQuery(id+"F0.wireOp",EDGE,"E11.MirrorCS"),sQuery(id+"F0.wireOp",EDGE,"E12.MirrorCS"),sQuery(id+"F0.wireOp",EDGE,"E13.MirrorCS"),sQuery(id+"F0.wireOp",EDGE,"E14.MirrorCS"),sQuery(id+"F0.wireOp",EDGE,"E16.MirrorCS"),sQuery(id+"F0.wireOp",EDGE,"E17.MirrorCS"),sQuery(id+"F0.wireOp",EDGE,"E18.MirrorCS"),sQuery(id+"F0.wireOp",EDGE,"E19.MirrorCS"),sQuery(id+"F0.wireOp",EDGE,"E20.MirrorCS"),sQuery(id+"F0.wireOp",EDGE,"E21.MirrorCS"),sQuery(id+"F0.wireOp",EDGE,"E22.MirrorCS"),sQuery(id+"F0.wireOp",EDGE,"E23.MirrorCS"),sQuery(id+"F0.wireOp",EDGE,"E25.MirrorCS"),sQuery(id+"F0.wireOp",EDGE,"E26.MirrorCS"),sQuery(id+"F0.wireOp",EDGE,"E27.MirrorCS"),sQuery(id+"F0.wireOp",EDGE,"E28.MirrorCS"),sQuery(id+"F0.wireOp",EDGE,"E29.MirrorCS"),sQuery(id+"F0.wireOp",EDGE,"E30.MirrorCS"),sQuery(id+"F0.wireOp",EDGE,"E31.MirrorCS"),sQuery(id+"F0.wireOp",EDGE,"E32.MirrorCS")])]});
            hole(context, id + "F12", {"style" : HoleStyle.C_SINK, "holeDiameter" : 2 * mm, "cSinkDiameter" : 4 * mm, "endStyle" : HoleEndStyle.THROUGH, "locations" : qUnion([Q0, Q1, Q2, Q3]), "scope" : qUnion([Q4]), "cSinkAngle" : 90 * degree});
        }
        {
            var Q0;
            Q0=makeQuery(id+"F11.imprint","IMPRINT",FACE,{"disambiguationData":[TD([[makeQuery(id+"F11.imprint","IMPRINT",EDGE,{"derivedFrom":sQuery(id+"F11.wireOp",EDGE,"E54.bottom")}),-1.0]])]});
            var Q1;
            Q1=makeQuery(id+"F11.imprint","IMPRINT",FACE,{"disambiguationData":[TD([[makeQuery(id+"F11.imprint","IMPRINT",EDGE,{"derivedFrom":sQuery(id+"F11.wireOp",EDGE,"E59.MirrorCS")}),1.0]])]});
            var Q2;
            Q2=makeQuery(id+"F11.imprint","IMPRINT",FACE,{"disambiguationData":[TD([[makeQuery(id+"F11.imprint","IMPRINT",EDGE,{"derivedFrom":sQuery(id+"F11.wireOp",EDGE,"E63.MirrorCS")}),1.0]])]});
            var Q3;
            Q3=makeQuery(id+"F11.imprint","IMPRINT",FACE,{"disambiguationData":[TD([[makeQuery(id+"F11.imprint","IMPRINT",EDGE,{"derivedFrom":sQuery(id+"F11.wireOp",EDGE,"E55.MirrorCS")}),-1.0]])]});
            extrude(context, id + "F13", {"entities" : qUnion([Q0, Q1, Q2, Q3]), "operationType" : NewBodyOperationType.ADD, "depth" : 6 * mm});
        }
    });
